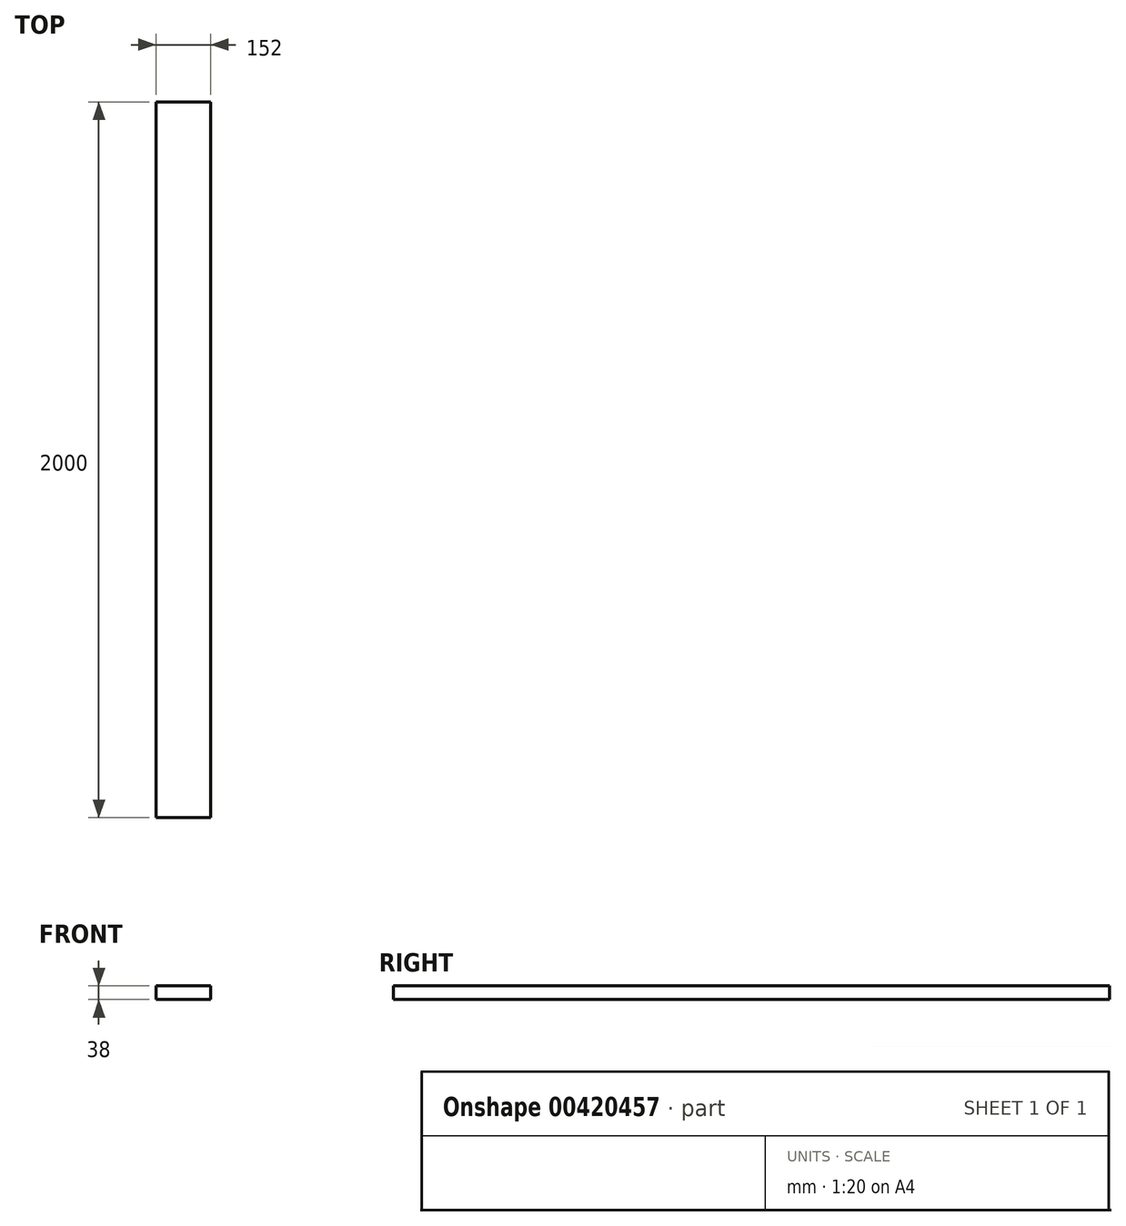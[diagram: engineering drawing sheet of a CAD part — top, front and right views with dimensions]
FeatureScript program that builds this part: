
annotation { "Feature Type Name" : "Feature", "Feature Type Description" : "" }
export const myFeature = defineFeature(function(context is Context, id is Id, definition is map)
    precondition{}
    {
        {
            var Q0;
            Q0=qCreatedBy(makeId("Front.planeOp"),FACE);
            var sketch = newSketch(context, id + "F0", { "sketchPlane" : qUnion([Q0])});
            skLineSegment(sketch, "E0.bottom", {"start": v(76, 19) * mm, "end": v(-76, 19) * mm});
            skLineSegment(sketch, "E0.top", {"start": v(76, -19) * mm, "end": v(-76, -19) * mm});
            skLineSegment(sketch, "E0.left", {"start": v(76, 19) * mm, "end": v(76, -19) * mm});
            skLineSegment(sketch, "E0.right", {"start": v(-76, 19) * mm, "end": v(-76, -19) * mm});
            skPoint(sketch, "E0.middle", {"position": v(0, 0) * mm});
            skSolve(sketch);
        }
        {
            var Q0;
            Q0=makeQuery(id+"F0.imprint","IMPRINT",FACE,{"disambiguationData":[TD([[makeQuery(id+"F0.imprint","IMPRINT",EDGE,{"derivedFrom":sQuery(id+"F0.wireOp",EDGE,"E0.bottom")}),1.0]])]});
            extrude(context, id + "F1", {"entities" : qUnion([Q0]), "endBound" : BoundingType.SYMMETRIC, "depth" : 2000 * mm});
        }
    });
